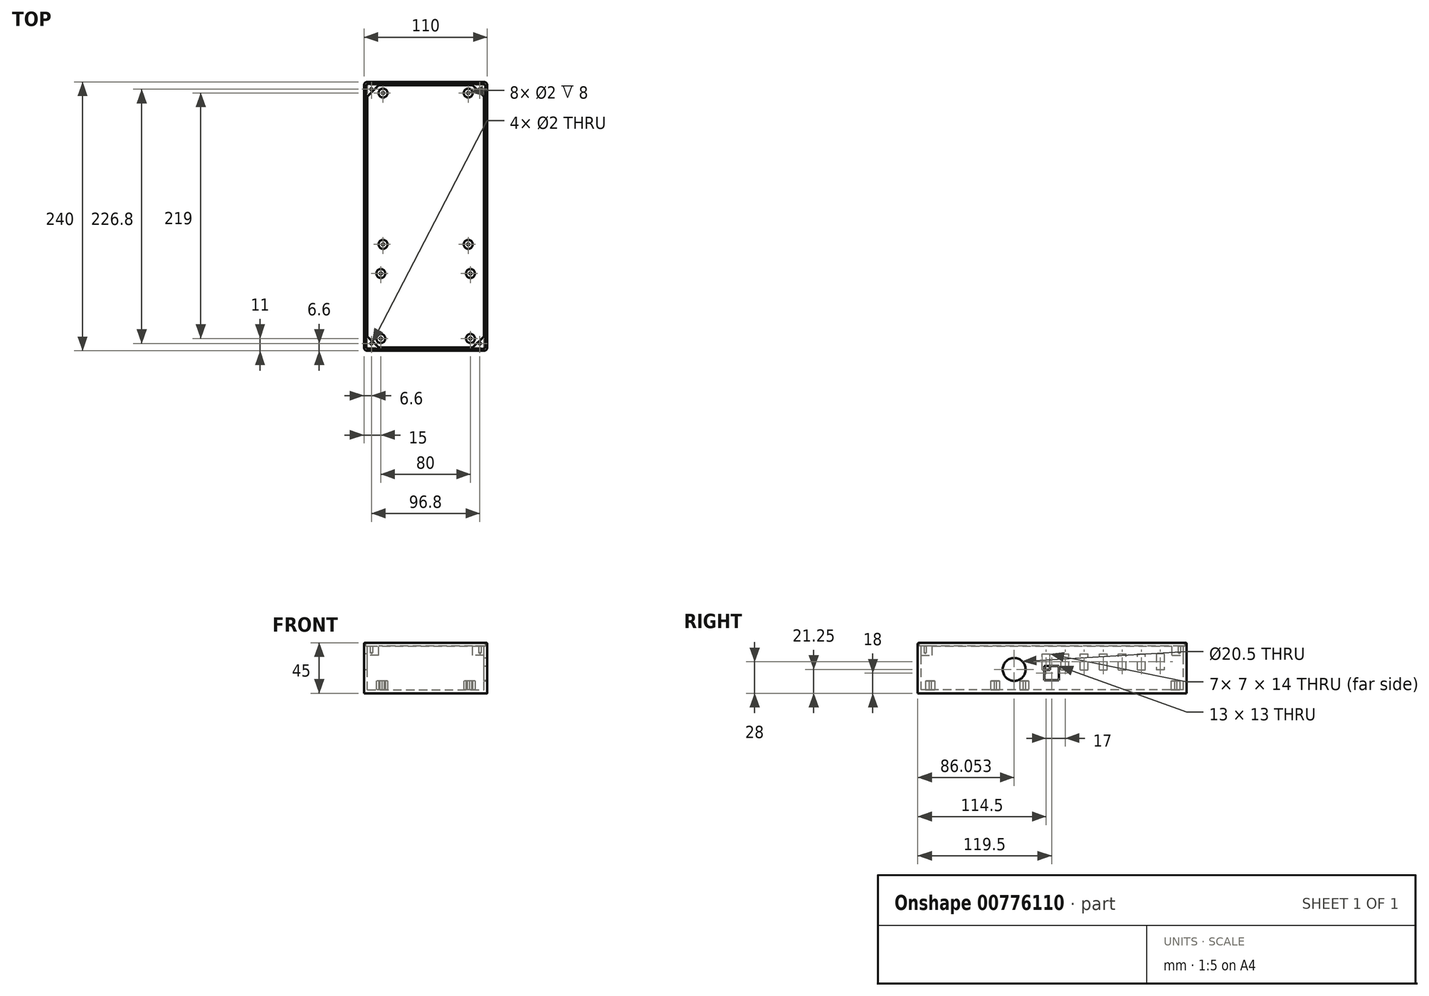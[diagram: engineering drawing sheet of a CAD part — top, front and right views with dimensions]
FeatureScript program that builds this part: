
annotation { "Feature Type Name" : "Feature", "Feature Type Description" : "" }
export const myFeature = defineFeature(function(context is Context, id is Id, definition is map)
    precondition{}
    {
        {
            var Q0;
            Q0=qCreatedBy(makeId("Top.planeOp"),FACE);
            var sketch = newSketch(context, id + "F0", { "sketchPlane" : qUnion([Q0])});
            skLineSegment(sketch, "E0.bottom", {"start": v(55, -120) * mm, "end": v(-55, -120) * mm});
            skLineSegment(sketch, "E0.top", {"start": v(55, 120) * mm, "end": v(-55, 120) * mm});
            skLineSegment(sketch, "E0.left", {"start": v(55, -120) * mm, "end": v(55, 120) * mm});
            skLineSegment(sketch, "E0.right", {"start": v(-55, -120) * mm, "end": v(-55, 120) * mm});
            skPoint(sketch, "E0.middle", {"position": v(0, 0) * mm});
            skSolve(sketch);
        }
        {
            var Q0;
            Q0=makeQuery(id+"F0.imprint","IMPRINT",FACE,{"disambiguationData":[TD([[makeQuery(id+"F0.imprint","IMPRINT",EDGE,{"derivedFrom":sQuery(id+"F0.wireOp",EDGE,"E0.bottom")}),-1.0]])]});
            extrude(context, id + "F1", {"entities" : qUnion([Q0]), "depth" : 45 * mm, "offsetDistance" : 25 * mm});
        }
        {
            var Q0;
            Q0=makeQuery(id+"F1.opExtrude","CAP_FACE",FACE,{"disambiguationData":[OSD([sQuery(id+"F0.wireOp",EDGE,"E0.bottom"),sQuery(id+"F0.wireOp",EDGE,"E0.top"),sQuery(id+"F0.wireOp",EDGE,"E0.left"),sQuery(id+"F0.wireOp",EDGE,"E0.right")])],"isStart":false});
            var sketch = newSketch(context, id + "F2", { "sketchPlane" : qUnion([Q0])});
            skLineSegment(sketch, "E1.bottom", {"start": v(52, -117) * mm, "end": v(-52, -117) * mm});
            skLineSegment(sketch, "E1.top", {"start": v(52, 117) * mm, "end": v(-52, 117) * mm});
            skLineSegment(sketch, "E1.left", {"start": v(52, -117) * mm, "end": v(52, 117) * mm});
            skLineSegment(sketch, "E1.right", {"start": v(-52, -117) * mm, "end": v(-52, 117) * mm});
            skPoint(sketch, "E1.middle", {"position": v(0, 0) * mm});
            skSolve(sketch);
        }
        {
            var Q0;
            Q0=qSketchRegion(id+"F2",true);
            var Q1;
            Q1=makeQuery(id+"F1.opExtrude","CAP_FACE",FACE,{"disambiguationData":[OSD([sQuery(id+"F0.wireOp",EDGE,"E0.bottom"),sQuery(id+"F0.wireOp",EDGE,"E0.top"),sQuery(id+"F0.wireOp",EDGE,"E0.left"),sQuery(id+"F0.wireOp",EDGE,"E0.right")])],"isStart":true});
            extrude(context, id + "F3", {"entities" : qUnion([Q0]), "operationType" : NewBodyOperationType.REMOVE, "endBound" : BoundingType.UP_TO_SURFACE, "oppositeDirection" : true, "depth" : 35 * mm, "endBoundEntityFace" : qUnion([Q1]), "hasOffset" : true, "offsetDistance" : 3 * mm});
        }
        {
            var Q0;
            Q0=makeQuery(id+"F1.opExtrude","CAP_FACE",FACE,{"disambiguationData":[OSD([sQuery(id+"F0.wireOp",EDGE,"E0.bottom"),sQuery(id+"F0.wireOp",EDGE,"E0.top"),sQuery(id+"F0.wireOp",EDGE,"E0.left"),sQuery(id+"F0.wireOp",EDGE,"E0.right")])],"isStart":false});
            var sketch = newSketch(context, id + "F4", { "sketchPlane" : qUnion([Q0])});
            skLineSegment(sketch, "E2.bottom", {"start": v(-53.4, 118.4) * mm, "end": v(53.4, 118.4) * mm});
            skLineSegment(sketch, "E2.top", {"start": v(-53.4, -118.4) * mm, "end": v(53.4, -118.4) * mm});
            skLineSegment(sketch, "E2.left", {"start": v(-53.4, 118.4) * mm, "end": v(-53.4, -118.4) * mm});
            skLineSegment(sketch, "E2.right", {"start": v(53.4, 118.4) * mm, "end": v(53.4, -118.4) * mm});
            skPoint(sketch, "E2.middle", {"position": v(0, 0) * mm});
            skSolve(sketch);
        }
        {
            var Q0;
            Q0=makeQuery(id+"F4.imprint","IMPRINT",FACE,{"disambiguationData":[TD([[makeQuery(id+"F4.imprint","IMPRINT",EDGE,{"derivedFrom":sQuery(id+"F4.wireOp",EDGE,"E2.bottom")}),-1.0]])]});
            var Q1;
            Q1=qSketchRegion(id+"F6",true);
            var Q2;
            Q2=makeQuery(id+"F3.boolean.opBoolean","COPY",FACE,{"derivedFrom":makeQuery(id+"F3.opExtrude","SWEPT_FACE",FACE,{"disambiguationData":[OSD([sQuery(id+"F2.wireOp",EDGE,"E1.left")])]})});
            extrude(context, id + "F5", {"entities" : qUnion([Q0, Q1]), "operationType" : NewBodyOperationType.REMOVE, "oppositeDirection" : true, "depth" : 3 * mm, "endBoundEntityFace" : qUnion([Q2]), "offsetDistance" : 25 * mm});
        }
        {
            var Q0;
            Q0=makeQuery(id+"F3.boolean.opBoolean","COPY",FACE,{"derivedFrom":makeQuery(id+"F3.opExtrude","CAP_FACE",FACE,{"disambiguationData":[OSD([sQuery(id+"F2.wireOp",EDGE,"E1.bottom"),sQuery(id+"F2.wireOp",EDGE,"E1.top"),sQuery(id+"F2.wireOp",EDGE,"E1.left"),sQuery(id+"F2.wireOp",EDGE,"E1.right")])],"isStart":false})});
            var sketch = newSketch(context, id + "F6", { "sketchPlane" : qUnion([Q0])});
            skCircle(sketch, "E3", {"center": v(-38, 110) * mm, "radius": 4 * mm});
            skCircle(sketch, "E4", {"center": v(-38, 110) * mm, "radius": 1 * mm});
            skCircle(sketch, "E5", {"center": v(38, 110) * mm, "radius": 4 * mm});
            skCircle(sketch, "E6", {"center": v(38, 110) * mm, "radius": 1 * mm});
            skCircle(sketch, "E7", {"center": v(-38, -25) * mm, "radius": 4 * mm});
            skCircle(sketch, "E8", {"center": v(-38, -25) * mm, "radius": 1 * mm});
            skCircle(sketch, "E9", {"center": v(38, -25) * mm, "radius": 4 * mm});
            skCircle(sketch, "E10", {"center": v(38, -25) * mm, "radius": 1 * mm});
            skCircle(sketch, "E11", {"center": v(-40, -51) * mm, "radius": 4 * mm});
            skCircle(sketch, "E12", {"center": v(40, -51) * mm, "radius": 4 * mm});
            skCircle(sketch, "E13", {"center": v(-40, -109) * mm, "radius": 4 * mm});
            skCircle(sketch, "E14", {"center": v(40, -109) * mm, "radius": 4 * mm});
            skCircle(sketch, "E15", {"center": v(-40, -51) * mm, "radius": 1 * mm});
            skCircle(sketch, "E16", {"center": v(40, -51) * mm, "radius": 1 * mm});
            skCircle(sketch, "E17", {"center": v(-40, -109) * mm, "radius": 1 * mm});
            skCircle(sketch, "E18", {"center": v(40, -109) * mm, "radius": 1 * mm});
            skSolve(sketch);
        }
        {
            var Q0;
            Q0=makeQuery(id+"F6.imprint","IMPRINT",FACE,{"disambiguationData":[TD([[makeQuery(id+"F6.imprint","IMPRINT",EDGE,{"derivedFrom":sQuery(id+"F6.wireOp",EDGE,"E3")}),1.0]])]});
            var Q1;
            Q1=makeQuery(id+"F6.imprint","IMPRINT",FACE,{"disambiguationData":[TD([[makeQuery(id+"F6.imprint","IMPRINT",EDGE,{"derivedFrom":sQuery(id+"F6.wireOp",EDGE,"E5")}),1.0]])]});
            var Q2;
            Q2=makeQuery(id+"F6.imprint","IMPRINT",FACE,{"disambiguationData":[TD([[makeQuery(id+"F6.imprint","IMPRINT",EDGE,{"derivedFrom":sQuery(id+"F6.wireOp",EDGE,"E7")}),1.0]])]});
            var Q3;
            Q3=makeQuery(id+"F6.imprint","IMPRINT",FACE,{"disambiguationData":[TD([[makeQuery(id+"F6.imprint","IMPRINT",EDGE,{"derivedFrom":sQuery(id+"F6.wireOp",EDGE,"E9")}),1.0]])]});
            var Q4;
            Q4=makeQuery(id+"F6.imprint","IMPRINT",FACE,{"disambiguationData":[TD([[makeQuery(id+"F6.imprint","IMPRINT",EDGE,{"derivedFrom":sQuery(id+"F6.wireOp",EDGE,"E11")}),1.0]])]});
            var Q5;
            Q5=makeQuery(id+"F6.imprint","IMPRINT",FACE,{"disambiguationData":[TD([[makeQuery(id+"F6.imprint","IMPRINT",EDGE,{"derivedFrom":sQuery(id+"F6.wireOp",EDGE,"E12")}),1.0]])]});
            var Q6;
            Q6=makeQuery(id+"F6.imprint","IMPRINT",FACE,{"disambiguationData":[TD([[makeQuery(id+"F6.imprint","IMPRINT",EDGE,{"derivedFrom":sQuery(id+"F6.wireOp",EDGE,"E13")}),1.0]])]});
            var Q7;
            Q7=makeQuery(id+"F6.imprint","IMPRINT",FACE,{"disambiguationData":[TD([[makeQuery(id+"F6.imprint","IMPRINT",EDGE,{"derivedFrom":sQuery(id+"F6.wireOp",EDGE,"E14")}),1.0]])]});
            extrude(context, id + "F7", {"entities" : qUnion([Q0, Q1, Q2, Q3, Q4, Q5, Q6, Q7]), "operationType" : NewBodyOperationType.ADD, "depth" : 8 * mm, "offsetDistance" : 25 * mm});
        }
        {
            var Q0;
            Q0=makeQuery(id+"F1.opExtrude","SWEPT_FACE",FACE,{"disambiguationData":[OSD([sQuery(id+"F0.wireOp",EDGE,"E0.left")])]});
            var sketch = newSketch(context, id + "F8", { "sketchPlane" : qUnion([Q0])});
            skLineSegment(sketch, "E19.bottom", {"start": v(-7, 24.5) * mm, "end": v(6, 24.5) * mm});
            skLineSegment(sketch, "E19.top", {"start": v(-7, 11.5) * mm, "end": v(6, 11.5) * mm});
            skLineSegment(sketch, "E19.left", {"start": v(-7, 24.5) * mm, "end": v(-7, 11.5) * mm});
            skLineSegment(sketch, "E19.right", {"start": v(6, 24.5) * mm, "end": v(6, 11.5) * mm});
            skPoint(sketch, "E20.0", {"position": v(-25, 3) * mm});
            skLineSegment(sketch, "E21.0.0", {"start": v(-29, 11) * mm, "end": v(-21, 11) * mm});
            skSolve(sketch);
        }
        {
            var Q0;
            Q0=makeQuery(id+"F8.imprint","IMPRINT",FACE,{"disambiguationData":[TD([[makeQuery(id+"F8.imprint","IMPRINT",EDGE,{"derivedFrom":sQuery(id+"F8.wireOp",EDGE,"E19.bottom")}),-1.0]])]});
            var Q1;
            Q1=makeQuery(id+"F3.boolean.opBoolean","COPY",FACE,{"derivedFrom":makeQuery(id+"F3.opExtrude","SWEPT_FACE",FACE,{"disambiguationData":[OSD([sQuery(id+"F2.wireOp",EDGE,"E1.left")])]})});
            extrude(context, id + "F9", {"entities" : qUnion([Q0]), "operationType" : NewBodyOperationType.REMOVE, "endBound" : BoundingType.UP_TO_SURFACE, "oppositeDirection" : true, "depth" : 25 * mm, "endBoundEntityFace" : qUnion([Q1]), "offsetDistance" : 25 * mm});
        }
        {
            var Q0;
            Q0=makeQuery(id+"F1.opExtrude","SWEPT_FACE",FACE,{"disambiguationData":[OSD([sQuery(id+"F0.wireOp",EDGE,"E0.right")])]});
            var sketch = newSketch(context, id + "F10", { "sketchPlane" : qUnion([Q0])});
            skLineSegment(sketch, "E22.bottom", {"start": v(-100, 35) * mm, "end": v(-93, 35) * mm});
            skLineSegment(sketch, "E22.top", {"start": v(-100, 21) * mm, "end": v(-93, 21) * mm});
            skLineSegment(sketch, "E22.left", {"start": v(-100, 35) * mm, "end": v(-100, 21) * mm});
            skLineSegment(sketch, "E22.right", {"start": v(-93, 35) * mm, "end": v(-93, 21) * mm});
            skLineSegment(sketch, "E23.bottom", {"start": v(-76, 21) * mm, "end": v(-83, 21) * mm});
            skLineSegment(sketch, "E23.top", {"start": v(-76, 35) * mm, "end": v(-83, 35) * mm});
            skLineSegment(sketch, "E23.left", {"start": v(-76, 21) * mm, "end": v(-76, 35) * mm});
            skLineSegment(sketch, "E23.right", {"start": v(-83, 21) * mm, "end": v(-83, 35) * mm});
            skPoint(sketch, "E23.middle", {"position": v(-79.5, 28) * mm});
            skLineSegment(sketch, "E24.bottom", {"start": v(-59, 21) * mm, "end": v(-66, 21) * mm});
            skLineSegment(sketch, "E24.top", {"start": v(-59, 35) * mm, "end": v(-66, 35) * mm});
            skLineSegment(sketch, "E24.left", {"start": v(-59, 21) * mm, "end": v(-59, 35) * mm});
            skLineSegment(sketch, "E24.right", {"start": v(-66, 21) * mm, "end": v(-66, 35) * mm});
            skPoint(sketch, "E24.middle", {"position": v(-62.5, 28) * mm});
            skLineSegment(sketch, "E25.bottom", {"start": v(-42, 21) * mm, "end": v(-49, 21) * mm});
            skLineSegment(sketch, "E25.top", {"start": v(-42, 35) * mm, "end": v(-49, 35) * mm});
            skLineSegment(sketch, "E25.left", {"start": v(-42, 21) * mm, "end": v(-42, 35) * mm});
            skLineSegment(sketch, "E25.right", {"start": v(-49, 21) * mm, "end": v(-49, 35) * mm});
            skPoint(sketch, "E25.middle", {"position": v(-45.5, 28) * mm});
            skLineSegment(sketch, "E26.bottom", {"start": v(9, 21) * mm, "end": v(2, 21) * mm});
            skLineSegment(sketch, "E26.top", {"start": v(9, 35) * mm, "end": v(2, 35) * mm});
            skLineSegment(sketch, "E26.left", {"start": v(9, 21) * mm, "end": v(9, 35) * mm});
            skLineSegment(sketch, "E26.right", {"start": v(2, 21) * mm, "end": v(2, 35) * mm});
            skPoint(sketch, "E26.middle", {"position": v(5.5, 28) * mm});
            skLineSegment(sketch, "E27.bottom", {"start": v(-8, 21) * mm, "end": v(-15, 21) * mm});
            skLineSegment(sketch, "E27.top", {"start": v(-8, 35) * mm, "end": v(-15, 35) * mm});
            skLineSegment(sketch, "E27.left", {"start": v(-8, 21) * mm, "end": v(-8, 35) * mm});
            skLineSegment(sketch, "E27.right", {"start": v(-15, 21) * mm, "end": v(-15, 35) * mm});
            skPoint(sketch, "E27.middle", {"position": v(-11.5, 28) * mm});
            skLineSegment(sketch, "E28.bottom", {"start": v(-25, 21) * mm, "end": v(-32, 21) * mm});
            skLineSegment(sketch, "E28.top", {"start": v(-25, 35) * mm, "end": v(-32, 35) * mm});
            skLineSegment(sketch, "E28.left", {"start": v(-25, 21) * mm, "end": v(-25, 35) * mm});
            skLineSegment(sketch, "E28.right", {"start": v(-32, 21) * mm, "end": v(-32, 35) * mm});
            skPoint(sketch, "E28.middle", {"position": v(-28.5, 28) * mm});
            skSolve(sketch);
        }
        {
            var Q0;
            Q0=makeQuery(id+"F10.imprint","IMPRINT",FACE,{"disambiguationData":[TD([[makeQuery(id+"F10.imprint","IMPRINT",EDGE,{"derivedFrom":sQuery(id+"F10.wireOp",EDGE,"E24.bottom")}),-1.0]])]});
            var Q1;
            Q1=makeQuery(id+"F10.imprint","IMPRINT",FACE,{"disambiguationData":[TD([[makeQuery(id+"F10.imprint","IMPRINT",EDGE,{"derivedFrom":sQuery(id+"F10.wireOp",EDGE,"E25.bottom")}),-1.0]])]});
            var Q2;
            Q2=makeQuery(id+"F10.imprint","IMPRINT",FACE,{"disambiguationData":[TD([[makeQuery(id+"F10.imprint","IMPRINT",EDGE,{"derivedFrom":sQuery(id+"F10.wireOp",EDGE,"E28.bottom")}),-1.0]])]});
            var Q3;
            Q3=makeQuery(id+"F10.imprint","IMPRINT",FACE,{"disambiguationData":[TD([[makeQuery(id+"F10.imprint","IMPRINT",EDGE,{"derivedFrom":sQuery(id+"F10.wireOp",EDGE,"E27.bottom")}),-1.0]])]});
            var Q4;
            Q4=makeQuery(id+"F10.imprint","IMPRINT",FACE,{"disambiguationData":[TD([[makeQuery(id+"F10.imprint","IMPRINT",EDGE,{"derivedFrom":sQuery(id+"F10.wireOp",EDGE,"E26.bottom")}),-1.0]])]});
            var Q5;
            Q5=makeQuery(id+"F10.imprint","IMPRINT",FACE,{"disambiguationData":[TD([[makeQuery(id+"F10.imprint","IMPRINT",EDGE,{"derivedFrom":sQuery(id+"F10.wireOp",EDGE,"E23.bottom")}),-1.0]])]});
            var Q6;
            Q6=makeQuery(id+"F10.imprint","IMPRINT",FACE,{"disambiguationData":[TD([[makeQuery(id+"F10.imprint","IMPRINT",EDGE,{"derivedFrom":sQuery(id+"F10.wireOp",EDGE,"E22.bottom")}),-1.0]])]});
            var Q7;
            Q7=makeQuery(id+"F3.boolean.opBoolean","COPY",FACE,{"derivedFrom":makeQuery(id+"F3.opExtrude","SWEPT_FACE",FACE,{"disambiguationData":[OSD([sQuery(id+"F2.wireOp",EDGE,"E1.right")])]})});
            extrude(context, id + "F11", {"entities" : qUnion([Q0, Q1, Q2, Q3, Q4, Q5, Q6]), "operationType" : NewBodyOperationType.REMOVE, "endBound" : BoundingType.UP_TO_SURFACE, "oppositeDirection" : true, "depth" : 25 * mm, "endBoundEntityFace" : qUnion([Q7]), "offsetDistance" : 25 * mm});
        }
        {
            var Q0;
            Q0=makeQuery(id+"F1.opExtrude","SWEPT_EDGE",EDGE,{"disambiguationData":[OSD([sQuery(id+"F0.wireOp",EDGE,"E0.bottom"),sQuery(id+"F0.wireOp",EDGE,"E0.right")])]});
            var Q1;
            Q1=makeQuery(id+"F1.opExtrude","SWEPT_EDGE",EDGE,{"disambiguationData":[OSD([sQuery(id+"F0.wireOp",EDGE,"E0.bottom"),sQuery(id+"F0.wireOp",EDGE,"E0.left")])]});
            var Q2;
            Q2=makeQuery(id+"F1.opExtrude","SWEPT_EDGE",EDGE,{"disambiguationData":[OSD([sQuery(id+"F0.wireOp",EDGE,"E0.top"),sQuery(id+"F0.wireOp",EDGE,"E0.right")])]});
            var Q3;
            Q3=makeQuery(id+"F1.opExtrude","SWEPT_EDGE",EDGE,{"disambiguationData":[OSD([sQuery(id+"F0.wireOp",EDGE,"E0.top"),sQuery(id+"F0.wireOp",EDGE,"E0.left")])]});
            fillet(context, id + "F12", {"entities" : qUnion([Q0, Q1, Q2, Q3]), "radius" : 3 * mm, "tangentPropagation" : true, "allowEdgeOverflow" : false});
        }
        {
            var Q0;
            Q0=makeQuery(id+"F5.boolean.opBoolean","COPY",EDGE,{"derivedFrom":makeQuery(id+"F5.opExtrude","SWEPT_EDGE",EDGE,{"disambiguationData":[OSD([sQuery(id+"F4.wireOp",EDGE,"E2.bottom"),sQuery(id+"F4.wireOp",EDGE,"E2.left")])]})});
            var Q1;
            Q1=makeQuery(id+"F5.boolean.opBoolean","COPY",EDGE,{"derivedFrom":makeQuery(id+"F5.opExtrude","SWEPT_EDGE",EDGE,{"disambiguationData":[OSD([sQuery(id+"F4.wireOp",EDGE,"E2.bottom"),sQuery(id+"F4.wireOp",EDGE,"E2.right")])]})});
            var Q2;
            Q2=makeQuery(id+"F5.boolean.opBoolean","COPY",EDGE,{"derivedFrom":makeQuery(id+"F5.opExtrude","SWEPT_EDGE",EDGE,{"disambiguationData":[OSD([sQuery(id+"F4.wireOp",EDGE,"E2.top"),sQuery(id+"F4.wireOp",EDGE,"E2.right")])]})});
            var Q3;
            Q3=makeQuery(id+"F5.boolean.opBoolean","COPY",EDGE,{"derivedFrom":makeQuery(id+"F5.opExtrude","SWEPT_EDGE",EDGE,{"disambiguationData":[OSD([sQuery(id+"F4.wireOp",EDGE,"E2.top"),sQuery(id+"F4.wireOp",EDGE,"E2.left")])]})});
            fillet(context, id + "F13", {"entities" : qUnion([Q0, Q1, Q2, Q3]), "radius" : 3 * mm, "tangentPropagation" : true, "allowEdgeOverflow" : false});
        }
        {
            var Q0;
            Q0=makeQuery(id+"F5.boolean.opBoolean","COPY",FACE,{"derivedFrom":makeQuery(id+"F5.opExtrude","CAP_FACE",FACE,{"disambiguationData":[OSD([sQuery(id+"F2.wireOp",EDGE,"E1.bottom"),sQuery(id+"F2.wireOp",EDGE,"E1.top"),sQuery(id+"F2.wireOp",EDGE,"E1.left"),sQuery(id+"F2.wireOp",EDGE,"E1.right"),sQuery(id+"F4.wireOp",EDGE,"E2.bottom"),sQuery(id+"F4.wireOp",EDGE,"E2.top"),sQuery(id+"F4.wireOp",EDGE,"E2.left"),sQuery(id+"F4.wireOp",EDGE,"E2.right")])],"isStart":false})});
            var sketch = newSketch(context, id + "F14", { "sketchPlane" : qUnion([Q0])});
            skLineSegment(sketch, "E29", {"start": v(-52, 117) * mm, "end": v(-42, 117) * mm});
            skLineSegment(sketch, "E30", {"start": v(-42, 117) * mm, "end": v(-52, 107) * mm});
            skLineSegment(sketch, "E31", {"start": v(-52, 107) * mm, "end": v(-52, 117) * mm});
            skLineSegment(sketch, "E32", {"start": v(52, 117) * mm, "end": v(52, 107) * mm});
            skLineSegment(sketch, "E33", {"start": v(52, 107) * mm, "end": v(42, 117) * mm});
            skLineSegment(sketch, "E34", {"start": v(42, 117) * mm, "end": v(52, 117) * mm});
            skLineSegment(sketch, "E35", {"start": v(52, -117) * mm, "end": v(42, -117) * mm});
            skLineSegment(sketch, "E36", {"start": v(42, -117) * mm, "end": v(52, -107) * mm});
            skLineSegment(sketch, "E37", {"start": v(52, -107) * mm, "end": v(52, -117) * mm});
            skLineSegment(sketch, "E38", {"start": v(-52, -117) * mm, "end": v(-52, -107) * mm});
            skLineSegment(sketch, "E39", {"start": v(-52, -107) * mm, "end": v(-42, -117) * mm});
            skLineSegment(sketch, "E40", {"start": v(-42, -117) * mm, "end": v(-52, -117) * mm});
            skPoint(sketch, "E41", {"position": v(-48.4, 113.4) * mm});
            skPoint(sketch, "E42", {"position": v(48.4, 113.4) * mm});
            skPoint(sketch, "E43", {"position": v(48.4, -113.4) * mm});
            skPoint(sketch, "E44", {"position": v(-48.4, -113.4) * mm});
            skSolve(sketch);
        }
        {
            var Q0;
            Q0=qSketchRegion(id+"F14",true);
            extrude(context, id + "F15", {"entities" : qUnion([Q0]), "operationType" : NewBodyOperationType.ADD, "oppositeDirection" : true, "depth" : 8 * mm, "offsetDistance" : 25 * mm});
        }
        {
            var Q0;
            Q0=makeQuery(id+"F1.opExtrude","SWEPT_FACE",FACE,{"disambiguationData":[OSD([sQuery(id+"F0.wireOp",EDGE,"E0.left")])]});
            var sketch = newSketch(context, id + "F16", { "sketchPlane" : qUnion([Q0])});
            skCircle(sketch, "E45", {"center": v(-33.95, 21.25) * mm, "radius": 10.25 * mm});
            skLineSegment(sketch, "E46.0", {"start": v(-55, 11) * mm, "end": v(-47, 11) * mm});
            skLineSegment(sketch, "E47", {"start": v(-51, 11) * mm, "end": v(-13.25, 11) * mm});
            skSolve(sketch);
        }
        {
            var Q0;
            Q0=makeQuery(id+"F16.imprint","IMPRINT",FACE,{"disambiguationData":[TD([[makeQuery(id+"F16.imprint","IMPRINT",EDGE,{"derivedFrom":sQuery(id+"F16.wireOp",EDGE,"E45")}),1.0]])]});
            var Q1;
            Q1=makeQuery(id+"F3.boolean.opBoolean","COPY",FACE,{"derivedFrom":makeQuery(id+"F3.opExtrude","SWEPT_FACE",FACE,{"disambiguationData":[OSD([sQuery(id+"F2.wireOp",EDGE,"E1.left")])]})});
            extrude(context, id + "F17", {"entities" : qUnion([Q0]), "operationType" : NewBodyOperationType.REMOVE, "endBound" : BoundingType.UP_TO_SURFACE, "oppositeDirection" : true, "depth" : 25 * mm, "endBoundEntityFace" : qUnion([Q1]), "offsetDistance" : 25 * mm});
        }
        {
            var Q0;
            Q0=sQuery(id+"F14.wireOp",VERTEX,"E42");
            var Q1;
            Q1=sQuery(id+"F14.wireOp",VERTEX,"E41");
            var Q2;
            Q2=sQuery(id+"F14.wireOp",VERTEX,"E44");
            var Q3;
            Q3=sQuery(id+"F14.wireOp",VERTEX,"E43");
            var Q4;
            Q4=makeQuery(id+"F1.opExtrude","SWEPT_BODY",BODY,{"disambiguationData":[OSD([sQuery(id+"F0.wireOp",EDGE,"E0.bottom"),sQuery(id+"F0.wireOp",EDGE,"E0.top"),sQuery(id+"F0.wireOp",EDGE,"E0.left"),sQuery(id+"F0.wireOp",EDGE,"E0.right")])]});
            hole(context, id + "F18", {"style" : HoleStyle.SIMPLE, "endStyle" : HoleEndStyle.BLIND, "holeDiameter" : 2 * mm, "majorDiameter" : 5 * mm, "holeDepth" : 6 * mm, "isTappedThrough" : true, "tappedDepth" : 12 * mm, "tapClearance" : 3, "locations" : qUnion([Q0, Q1, Q2, Q3]), "scope" : qUnion([Q4])});
        }
        {
            var Q0;
            Q0=makeQuery(id+"F1.opExtrude","CAP_EDGE",EDGE,{"disambiguationData":[OSD([sQuery(id+"F0.wireOp",EDGE,"E0.bottom")])],"isStart":false});
            var Q1;
            Q1=makeQuery(id+"F17.boolean.opBoolean","COPY",EDGE,{"derivedFrom":makeQuery(id+"F17.opExtrude","CAP_EDGE",EDGE,{"disambiguationData":[OSD([sQuery(id+"F16.wireOp",EDGE,"E45")])],"isStart":true})});
            var Q2;
            Q2=makeQuery(id+"F9.boolean.opBoolean","COPY",EDGE,{"derivedFrom":makeQuery(id+"F9.opExtrude","CAP_EDGE",EDGE,{"disambiguationData":[OSD([sQuery(id+"F8.wireOp",EDGE,"E19.left")])],"isStart":true})});
            var Q3;
            Q3=makeQuery(id+"F9.boolean.opBoolean","COPY",EDGE,{"derivedFrom":makeQuery(id+"F9.opExtrude","CAP_EDGE",EDGE,{"disambiguationData":[OSD([sQuery(id+"F8.wireOp",EDGE,"E19.top")])],"isStart":true})});
            var Q4;
            Q4=makeQuery(id+"F9.boolean.opBoolean","COPY",EDGE,{"derivedFrom":makeQuery(id+"F9.opExtrude","CAP_EDGE",EDGE,{"disambiguationData":[OSD([sQuery(id+"F8.wireOp",EDGE,"E19.right")])],"isStart":true})});
            var Q5;
            Q5=makeQuery(id+"F9.boolean.opBoolean","COPY",EDGE,{"derivedFrom":makeQuery(id+"F9.opExtrude","CAP_EDGE",EDGE,{"disambiguationData":[OSD([sQuery(id+"F8.wireOp",EDGE,"E19.bottom")])],"isStart":true})});
            var Q6;
            Q6=makeQuery(id+"F11.boolean.opBoolean","COPY",EDGE,{"derivedFrom":makeQuery(id+"F11.opExtrude","CAP_EDGE",EDGE,{"disambiguationData":[OSD([sQuery(id+"F10.wireOp",EDGE,"E22.left")])],"isStart":true})});
            var Q7;
            Q7=makeQuery(id+"F11.boolean.opBoolean","COPY",EDGE,{"derivedFrom":makeQuery(id+"F11.opExtrude","CAP_EDGE",EDGE,{"disambiguationData":[OSD([sQuery(id+"F10.wireOp",EDGE,"E22.right")])],"isStart":true})});
            var Q8;
            Q8=makeQuery(id+"F11.boolean.opBoolean","COPY",EDGE,{"derivedFrom":makeQuery(id+"F11.opExtrude","CAP_EDGE",EDGE,{"disambiguationData":[OSD([sQuery(id+"F10.wireOp",EDGE,"E22.top")])],"isStart":true})});
            var Q9;
            Q9=makeQuery(id+"F11.boolean.opBoolean","COPY",EDGE,{"derivedFrom":makeQuery(id+"F11.opExtrude","CAP_EDGE",EDGE,{"disambiguationData":[OSD([sQuery(id+"F10.wireOp",EDGE,"E22.bottom")])],"isStart":true})});
            var Q10;
            Q10=makeQuery(id+"F11.boolean.opBoolean","COPY",EDGE,{"derivedFrom":makeQuery(id+"F11.opExtrude","CAP_EDGE",EDGE,{"disambiguationData":[OSD([sQuery(id+"F10.wireOp",EDGE,"E23.top")])],"isStart":true})});
            var Q11;
            Q11=makeQuery(id+"F11.boolean.opBoolean","COPY",EDGE,{"derivedFrom":makeQuery(id+"F11.opExtrude","CAP_EDGE",EDGE,{"disambiguationData":[OSD([sQuery(id+"F10.wireOp",EDGE,"E23.right")])],"isStart":true})});
            var Q12;
            Q12=makeQuery(id+"F11.boolean.opBoolean","COPY",EDGE,{"derivedFrom":makeQuery(id+"F11.opExtrude","CAP_EDGE",EDGE,{"disambiguationData":[OSD([sQuery(id+"F10.wireOp",EDGE,"E23.bottom")])],"isStart":true})});
            var Q13;
            Q13=makeQuery(id+"F11.boolean.opBoolean","COPY",EDGE,{"derivedFrom":makeQuery(id+"F11.opExtrude","CAP_EDGE",EDGE,{"disambiguationData":[OSD([sQuery(id+"F10.wireOp",EDGE,"E23.left")])],"isStart":true})});
            var Q14;
            Q14=makeQuery(id+"F11.boolean.opBoolean","COPY",EDGE,{"derivedFrom":makeQuery(id+"F11.opExtrude","CAP_EDGE",EDGE,{"disambiguationData":[OSD([sQuery(id+"F10.wireOp",EDGE,"E24.top")])],"isStart":true})});
            var Q15;
            Q15=makeQuery(id+"F11.boolean.opBoolean","COPY",EDGE,{"derivedFrom":makeQuery(id+"F11.opExtrude","CAP_EDGE",EDGE,{"disambiguationData":[OSD([sQuery(id+"F10.wireOp",EDGE,"E24.right")])],"isStart":true})});
            var Q16;
            Q16=makeQuery(id+"F11.boolean.opBoolean","COPY",EDGE,{"derivedFrom":makeQuery(id+"F11.opExtrude","CAP_EDGE",EDGE,{"disambiguationData":[OSD([sQuery(id+"F10.wireOp",EDGE,"E24.bottom")])],"isStart":true})});
            var Q17;
            Q17=makeQuery(id+"F11.boolean.opBoolean","COPY",EDGE,{"derivedFrom":makeQuery(id+"F11.opExtrude","CAP_EDGE",EDGE,{"disambiguationData":[OSD([sQuery(id+"F10.wireOp",EDGE,"E24.left")])],"isStart":true})});
            var Q18;
            Q18=makeQuery(id+"F11.boolean.opBoolean","COPY",EDGE,{"derivedFrom":makeQuery(id+"F11.opExtrude","CAP_EDGE",EDGE,{"disambiguationData":[OSD([sQuery(id+"F10.wireOp",EDGE,"E25.top")])],"isStart":true})});
            var Q19;
            Q19=makeQuery(id+"F11.boolean.opBoolean","COPY",EDGE,{"derivedFrom":makeQuery(id+"F11.opExtrude","CAP_EDGE",EDGE,{"disambiguationData":[OSD([sQuery(id+"F10.wireOp",EDGE,"E25.left")])],"isStart":true})});
            var Q20;
            Q20=makeQuery(id+"F11.boolean.opBoolean","COPY",EDGE,{"derivedFrom":makeQuery(id+"F11.opExtrude","CAP_EDGE",EDGE,{"disambiguationData":[OSD([sQuery(id+"F10.wireOp",EDGE,"E25.right")])],"isStart":true})});
            var Q21;
            Q21=makeQuery(id+"F11.boolean.opBoolean","COPY",EDGE,{"derivedFrom":makeQuery(id+"F11.opExtrude","CAP_EDGE",EDGE,{"disambiguationData":[OSD([sQuery(id+"F10.wireOp",EDGE,"E25.bottom")])],"isStart":true})});
            var Q22;
            Q22=makeQuery(id+"F11.boolean.opBoolean","COPY",EDGE,{"derivedFrom":makeQuery(id+"F11.opExtrude","CAP_EDGE",EDGE,{"disambiguationData":[OSD([sQuery(id+"F10.wireOp",EDGE,"E28.right")])],"isStart":true})});
            var Q23;
            Q23=makeQuery(id+"F11.boolean.opBoolean","COPY",EDGE,{"derivedFrom":makeQuery(id+"F11.opExtrude","CAP_EDGE",EDGE,{"disambiguationData":[OSD([sQuery(id+"F10.wireOp",EDGE,"E28.bottom")])],"isStart":true})});
            var Q24;
            Q24=makeQuery(id+"F11.boolean.opBoolean","COPY",EDGE,{"derivedFrom":makeQuery(id+"F11.opExtrude","CAP_EDGE",EDGE,{"disambiguationData":[OSD([sQuery(id+"F10.wireOp",EDGE,"E28.top")])],"isStart":true})});
            var Q25;
            Q25=makeQuery(id+"F11.boolean.opBoolean","COPY",EDGE,{"derivedFrom":makeQuery(id+"F11.opExtrude","CAP_EDGE",EDGE,{"disambiguationData":[OSD([sQuery(id+"F10.wireOp",EDGE,"E28.left")])],"isStart":true})});
            var Q26;
            Q26=makeQuery(id+"F11.boolean.opBoolean","COPY",EDGE,{"derivedFrom":makeQuery(id+"F11.opExtrude","CAP_EDGE",EDGE,{"disambiguationData":[OSD([sQuery(id+"F10.wireOp",EDGE,"E27.right")])],"isStart":true})});
            var Q27;
            Q27=makeQuery(id+"F11.boolean.opBoolean","COPY",EDGE,{"derivedFrom":makeQuery(id+"F11.opExtrude","CAP_EDGE",EDGE,{"disambiguationData":[OSD([sQuery(id+"F10.wireOp",EDGE,"E27.bottom")])],"isStart":true})});
            var Q28;
            Q28=makeQuery(id+"F11.boolean.opBoolean","COPY",EDGE,{"derivedFrom":makeQuery(id+"F11.opExtrude","CAP_EDGE",EDGE,{"disambiguationData":[OSD([sQuery(id+"F10.wireOp",EDGE,"E27.top")])],"isStart":true})});
            var Q29;
            Q29=makeQuery(id+"F11.boolean.opBoolean","COPY",EDGE,{"derivedFrom":makeQuery(id+"F11.opExtrude","CAP_EDGE",EDGE,{"disambiguationData":[OSD([sQuery(id+"F10.wireOp",EDGE,"E27.left")])],"isStart":true})});
            var Q30;
            Q30=makeQuery(id+"F11.boolean.opBoolean","COPY",EDGE,{"derivedFrom":makeQuery(id+"F11.opExtrude","CAP_EDGE",EDGE,{"disambiguationData":[OSD([sQuery(id+"F10.wireOp",EDGE,"E26.top")])],"isStart":true})});
            var Q31;
            Q31=makeQuery(id+"F11.boolean.opBoolean","COPY",EDGE,{"derivedFrom":makeQuery(id+"F11.opExtrude","CAP_EDGE",EDGE,{"disambiguationData":[OSD([sQuery(id+"F10.wireOp",EDGE,"E26.right")])],"isStart":true})});
            var Q32;
            Q32=makeQuery(id+"F11.boolean.opBoolean","COPY",EDGE,{"derivedFrom":makeQuery(id+"F11.opExtrude","CAP_EDGE",EDGE,{"disambiguationData":[OSD([sQuery(id+"F10.wireOp",EDGE,"E26.left")])],"isStart":true})});
            var Q33;
            Q33=makeQuery(id+"F11.boolean.opBoolean","COPY",EDGE,{"derivedFrom":makeQuery(id+"F11.opExtrude","CAP_EDGE",EDGE,{"disambiguationData":[OSD([sQuery(id+"F10.wireOp",EDGE,"E26.bottom")])],"isStart":true})});
            fillet(context, id + "F19", {"entities" : qUnion([Q0, Q1, Q2, Q3, Q4, Q5, Q6, Q7, Q8, Q9, Q10, Q11, Q12, Q13, Q14, Q15, Q16, Q17, Q18, Q19, Q20, Q21, Q22, Q23, Q24, Q25, Q26, Q27, Q28, Q29, Q30, Q31, Q32, Q33]), "radius" : 1 * mm, "tangentPropagation" : true, "allowEdgeOverflow" : false});
        }
    });
